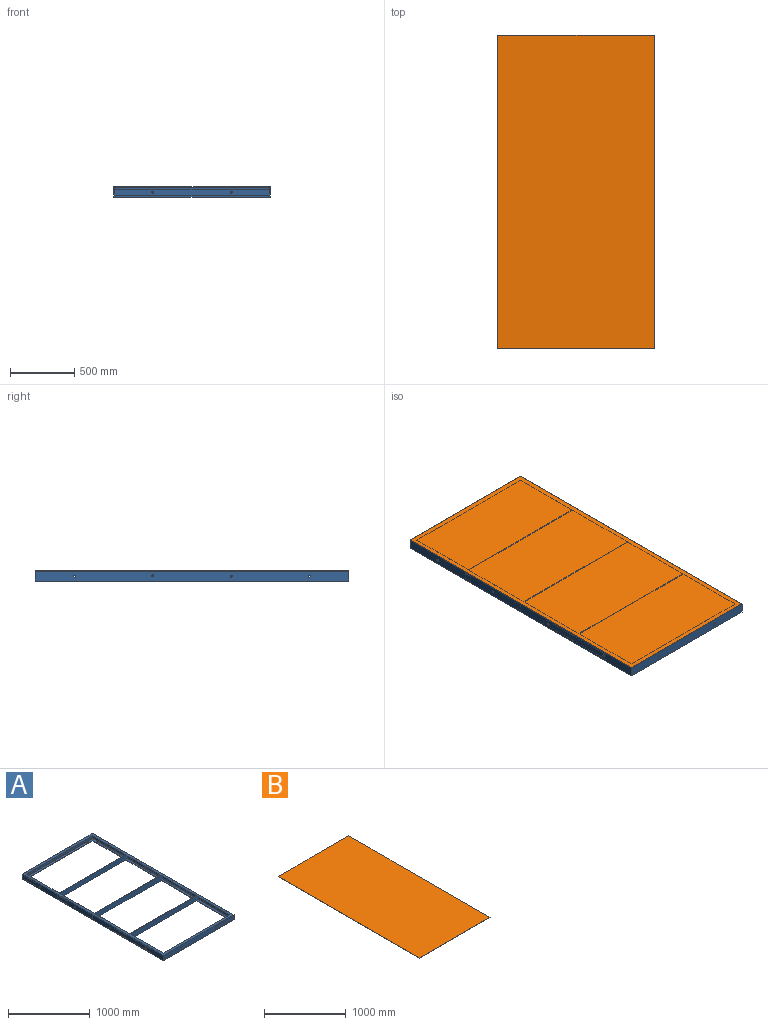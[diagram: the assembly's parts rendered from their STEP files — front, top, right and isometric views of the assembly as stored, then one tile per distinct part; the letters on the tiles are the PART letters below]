
ASSEMBLY  parts=2 mates=1
PART A: 122 faces, bbox 1219.4x2438.6x76.4 mm
  f0: cylinder r=2.54mm len=603.25mm, axis (0,1,0), area 2155.3mm2, adj f1,f8,f110,f113
  f1: plane 603.25x23.69mm, normal (0.16,0,-0.99), area 14489.9mm2, adj f0,f2,f110,f113
  f2: cylinder r=6.86mm len=603.25mm, axis (0,1,0), area 5814.6mm2, adj f1,f3,f110,f113
  f3: plane 603.25x45.45mm, normal (1,0,0), area 27220.2mm2, adj f2,f4,f106,f110,f113
  f4: cylinder r=6.86mm len=603.25mm, axis (0,1,0), area 5814.6mm2, adj f3,f5,f110,f113
  f5: plane 603.25x23.69mm, normal (0.16,0,0.99), area 14489.9mm2, adj f4,f6,f110,f113
  f6: cylinder r=2.54mm len=603.25mm, axis (0,1,0), area 2155.3mm2, adj f5,f7,f110,f113
  f7: plane 603.25x2.16mm, normal (1,0,0), area 1300.9mm2, adj f6,f64,f110,f113
  f8: plane 603.25x2.16mm, normal (1,0,0), area 1300.9mm2, adj f0,f66,f110,f113
  f9: cylinder r=2.54mm len=603.25mm, axis (0,-1,0), area 2155.3mm2, adj f10,f17,f110,f113
  f10: plane 603.25x23.69mm, normal (-0.16,0,-0.99), area 14489.9mm2, adj f9,f11,f110,f113
  f11: cylinder r=6.86mm len=603.25mm, axis (0,-1,0), area 5814.6mm2, adj f10,f12,f110,f113
  f12: plane 603.25x45.45mm, normal (-1,0,0), area 27220.2mm2, adj f11,f13,f102,f110,f113
  f13: cylinder r=6.86mm len=603.25mm, axis (0,-1,0), area 5814.6mm2, adj f12,f14,f110,f113
  f14: plane 603.25x23.69mm, normal (-0.16,0,0.99), area 14489.9mm2, adj f13,f15,f110,f113
  f15: cylinder r=2.54mm len=603.25mm, axis (0,-1,0), area 2155.3mm2, adj f14,f16,f110,f113
  f16: plane 603.25x2.16mm, normal (-1,0,0), area 1300.9mm2, adj f15,f64,f110,f113
  f17: plane 603.25x2.16mm, normal (-1,0,0), area 1300.9mm2, adj f9,f66,f110,f113
  f18: cylinder r=2.54mm len=603.25mm, axis (0,1,0), area 2155.3mm2, adj f19,f26,f108,f111
  f19: plane 603.25x23.69mm, normal (0.16,0,-0.99), area 14489.9mm2, adj f18,f20,f108,f111
  f20: cylinder r=6.86mm len=603.25mm, axis (0,1,0), area 5814.6mm2, adj f19,f21,f108,f111
  f21: plane 603.25x45.45mm, normal (1,0,0), area 27220.2mm2, adj f20,f22,f105,f108,f111
  f22: cylinder r=6.86mm len=603.25mm, axis (0,1,0), area 5814.6mm2, adj f21,f23,f108,f111
  f23: plane 603.25x23.69mm, normal (0.16,0,0.99), area 14489.9mm2, adj f22,f24,f108,f111
  f24: cylinder r=2.54mm len=603.25mm, axis (0,1,0), area 2155.3mm2, adj f23,f25,f108,f111
  f25: plane 603.25x2.16mm, normal (1,0,0), area 1300.9mm2, adj f24,f64,f108,f111
  f26: plane 603.25x2.16mm, normal (1,0,0), area 1300.9mm2, adj f18,f66,f108,f111
  f27: cylinder r=2.54mm len=603.25mm, axis (0,-1,0), area 2155.3mm2, adj f28,f35,f108,f111
  f28: plane 603.25x23.69mm, normal (-0.16,0,-0.99), area 14489.9mm2, adj f27,f29,f108,f111
  f29: cylinder r=6.86mm len=603.25mm, axis (0,-1,0), area 5814.6mm2, adj f28,f30,f108,f111
  f30: plane 603.25x45.45mm, normal (-1,0,0), area 27220.2mm2, adj f29,f31,f101,f108,f111
  f31: cylinder r=6.86mm len=603.25mm, axis (0,-1,0), area 5814.6mm2, adj f30,f32,f108,f111
  f32: plane 603.25x23.69mm, normal (-0.16,0,0.99), area 14489.9mm2, adj f31,f33,f108,f111
  f33: cylinder r=2.54mm len=603.25mm, axis (0,-1,0), area 2155.3mm2, adj f32,f34,f108,f111
  f34: plane 603.25x2.16mm, normal (-1,0,0), area 1300.9mm2, adj f33,f64,f108,f111
  f35: plane 603.25x2.16mm, normal (-1,0,0), area 1300.9mm2, adj f27,f66,f108,f111
  f36: cylinder r=2.54mm len=573.62mm, axis (0,1,0), area 2044.6mm2, adj f37,f44,f74,f109
  f37: plane 597.32x23.69mm, normal (0.16,0,-0.99), area 14062.8mm2, adj f36,f38,f73,f109
  f38: cylinder r=6.86mm len=603.05mm, axis (0,1,0), area 5792.9mm2, adj f37,f39,f72,f109
  f39: plane 603.05x45.45mm, normal (1,0,0), area 27211mm2, adj f38,f40,f71,f107,f109
  f40: cylinder r=6.86mm len=603.05mm, axis (0,1,0), area 5786.1mm2, adj f39,f41,f70,f109,f119
  f41: plane 597.48x23.86mm, normal (0.16,0,0.99), area 13868.8mm2, adj f40,f42,f69,f109,f119
  f42: cylinder r=2.54mm len=573.62mm, axis (0,1,0), area 2044.6mm2, adj f41,f43,f68,f109
  f43: plane 571.5x2.16mm, normal (1,0,0), area 1232.4mm2, adj f42,f64,f76,f109
  f44: plane 571.5x2.16mm, normal (1,0,0), area 1232.4mm2, adj f36,f66,f75,f109
  f45: cylinder r=2.54mm len=573.62mm, axis (0,-1,0), area 2044.6mm2, adj f46,f53,f74,f109
  f46: plane 597.32x23.69mm, normal (-0.16,0,-0.99), area 14062.8mm2, adj f45,f47,f73,f109
  f47: cylinder r=6.86mm len=603.05mm, axis (0,-1,0), area 5792.9mm2, adj f46,f48,f72,f109
  f48: plane 603.05x45.45mm, normal (-1,0,0), area 27211mm2, adj f47,f49,f71,f103,f109
  f49: cylinder r=6.86mm len=603.05mm, axis (0,-1,0), area 5786.1mm2, adj f48,f50,f70,f109,f121
  f50: plane 597.48x23.86mm, normal (-0.16,0,0.99), area 13868.8mm2, adj f49,f51,f69,f109,f121
  f51: cylinder r=2.54mm len=573.62mm, axis (0,-1,0), area 2044.6mm2, adj f50,f52,f68,f109
  f52: plane 571.5x2.16mm, normal (-1,0,0), area 1232.4mm2, adj f51,f64,f76,f109
  f53: plane 571.5x2.16mm, normal (-1,0,0), area 1232.4mm2, adj f45,f66,f75,f109
  f54: plane 1219.2x76.2mm, normal (0,-1,0), area 92507.2mm2, adj f64,f65,f66,f94,f98,f99
  f55: plane 1219.2x76.2mm, normal (0,1,0), area 92507.2mm2, adj f64,f65,f66,f94,f96,f97
  f56: cylinder r=2.54mm len=567.27mm, axis (0,1,0), area 2021.9mm2, adj f57,f67,f77,f112
  f57: plane 590.97x23.69mm, normal (0.16,0,-0.99), area 13910.3mm2, adj f56,f58,f78,f112
  f58: cylinder r=6.86mm len=596.7mm, axis (0,1,0), area 5731.7mm2, adj f57,f59,f79,f112
  f59: plane 596.7x45.45mm, normal (1,0,0), area 26922.4mm2, adj f58,f60,f80,f104,f112
  f60: cylinder r=6.86mm len=596.7mm, axis (0,1,0), area 5724.9mm2, adj f59,f61,f81,f112,f120
  f61: plane 591.13x23.86mm, normal (0.16,0,0.99), area 13716.3mm2, adj f60,f62,f82,f112,f120
  f62: cylinder r=2.54mm len=567.27mm, axis (0,1,0), area 2021.9mm2, adj f61,f63,f83,f112
  f63: plane 565.15x2.16mm, normal (1,0,0), area 1218.7mm2, adj f62,f64,f84,f112
  f64: plane 2438.4x1219.2mm, normal (0,0,-1), area 293093.4mm2, adj f7,f16,f25,f34,f43,f52,f54,f55
  f65: plane 2438.4x76.2mm, normal (-1,0,0), area 185014.3mm2, adj f54,f55,f64,f66,f104,f105,f106,f107
  f66: plane 2438.4x1219.2mm, normal (0,0,1), area 294676.8mm2, adj f8,f17,f26,f35,f44,f53,f54,f55
  f67: plane 565.15x2.16mm, normal (1,0,0), area 1218.7mm2, adj f56,f66,f85,f112
  f68: cylinder r=2.54mm len=1147.25mm, axis (1,0,0), area 4089.2mm2, adj f42,f51,f69,f76
  f69: plane 1194.63x23.69mm, normal (0,0.16,0.99), area 27737.6mm2, adj f41,f50,f68,f70,f117,f118
  f70: cylinder r=6.86mm len=1206.09mm, axis (1,0,0), area 11572.3mm2, adj f40,f49,f69,f71,f117,f118
  f71: plane 1206.09x45.45mm, normal (0,1,0), area 54422mm2, adj f39,f48,f70,f72,f98,f99
  f72: cylinder r=6.86mm len=1206.09mm, axis (1,0,0), area 11585.8mm2, adj f38,f47,f71,f73
  f73: plane 1194.63x23.69mm, normal (0,0.16,-0.99), area 28125.6mm2, adj f37,f46,f72,f74
  f74: cylinder r=2.54mm len=1147.25mm, axis (1,0,0), area 4089.2mm2, adj f36,f45,f73,f75
  f75: plane 1143x2.16mm, normal (0,1,0), area 2464.8mm2, adj f44,f53,f66,f74
  f76: plane 1143x2.16mm, normal (0,1,0), area 2464.8mm2, adj f43,f52,f64,f68
  f77: cylinder r=2.54mm len=1147.25mm, axis (1,0,0), area 4089.2mm2, adj f56,f78,f85,f86
  f78: plane 1194.63x23.69mm, normal (0,-0.16,-0.99), area 28125.6mm2, adj f57,f77,f79,f87
  f79: cylinder r=6.86mm len=1206.09mm, axis (1,0,0), area 11585.8mm2, adj f58,f78,f80,f88
  f80: plane 1206.09x45.45mm, normal (0,-1,0), area 54422mm2, adj f59,f79,f81,f89,f96,f97
  f81: cylinder r=6.86mm len=1206.09mm, axis (1,0,0), area 11572.3mm2, adj f60,f80,f82,f90,f115,f116
  f82: plane 1194.63x23.69mm, normal (0,-0.16,0.99), area 27737.6mm2, adj f61,f81,f83,f91,f115,f116
  f83: cylinder r=2.54mm len=1147.25mm, axis (1,0,0), area 4089.2mm2, adj f62,f82,f84,f92
  f84: plane 1143x2.16mm, normal (0,-1,0), area 2464.8mm2, adj f63,f64,f83,f93
  f85: plane 1143x2.16mm, normal (0,-1,0), area 2464.8mm2, adj f66,f67,f77,f95
  f86: cylinder r=2.54mm len=567.27mm, axis (0,-1,0), area 2021.9mm2, adj f77,f87,f95,f112
  f87: plane 590.97x23.69mm, normal (-0.16,0,-0.99), area 13910.3mm2, adj f78,f86,f88,f112
  f88: cylinder r=6.86mm len=596.7mm, axis (0,-1,0), area 5731.7mm2, adj f79,f87,f89,f112
  f89: plane 596.7x45.45mm, normal (-1,0,0), area 26922.4mm2, adj f80,f88,f90,f100,f112
  f90: cylinder r=6.86mm len=596.7mm, axis (0,-1,0), area 5724.9mm2, adj f81,f89,f91,f112,f114
  f91: plane 591.13x23.86mm, normal (-0.16,0,0.99), area 13716.3mm2, adj f82,f90,f92,f112,f114
  f92: cylinder r=2.54mm len=567.27mm, axis (0,-1,0), area 2021.9mm2, adj f83,f91,f93,f112
  f93: plane 565.15x2.16mm, normal (-1,0,0), area 1218.7mm2, adj f64,f84,f92,f112
  f94: plane 2438.4x76.2mm, normal (1,0,0), area 185014.3mm2, adj f54,f55,f64,f66,f100,f101,f102,f103
  f95: plane 565.15x2.16mm, normal (-1,0,0), area 1218.7mm2, adj f66,f85,f86,f112
  f96: cylinder r=7.94mm len=15.88mm, axis (0,-1,0), area 326.8mm2, adj f55,f80
  f97: cylinder r=7.94mm len=15.88mm, axis (0,-1,0), area 326.8mm2, adj f55,f80
  f98: cylinder r=7.94mm len=15.88mm, axis (0,-1,0), area 326.8mm2, adj f54,f71
  f99: cylinder r=7.94mm len=15.88mm, axis (0,-1,0), area 326.8mm2, adj f54,f71
  f100: cylinder r=7.94mm len=15.88mm, axis (1,0,0), area 326.8mm2, adj f89,f94
  f101: cylinder r=7.94mm len=15.88mm, axis (1,0,0), area 326.8mm2, adj f30,f94
  f102: cylinder r=7.94mm len=15.88mm, axis (1,0,0), area 326.8mm2, adj f12,f94
  f103: cylinder r=7.94mm len=15.88mm, axis (1,0,0), area 326.8mm2, adj f48,f94
  f104: cylinder r=7.94mm len=15.88mm, axis (1,0,0), area 326.8mm2, adj f59,f65
  f105: cylinder r=7.94mm len=15.88mm, axis (1,0,0), area 326.8mm2, adj f21,f65
  f106: cylinder r=7.94mm len=15.88mm, axis (1,0,0), area 326.8mm2, adj f3,f65
  f107: cylinder r=7.94mm len=15.88mm, axis (1,0,0), area 326.8mm2, adj f39,f65
  f108: plane 1206.09x76.2mm, normal (0,1,0), area 91005.5mm2, adj f18,f19,f20,f21,f22,f23,f24,f25
  f109: plane 1206.09x76.2mm, normal (0,-1,0), area 91005.5mm2, adj f36,f37,f38,f39,f40,f41,f42,f43
  f110: plane 1206.09x76.2mm, normal (0,1,0), area 91005.5mm2, adj f0,f1,f2,f3,f4,f5,f6,f7
  f111: plane 1206.09x76.2mm, normal (0,-1,0), area 91005.5mm2, adj f18,f19,f20,f21,f22,f23,f24,f25
  f112: plane 1206.09x76.2mm, normal (0,1,0), area 91005.5mm2, adj f56,f57,f58,f59,f60,f61,f62,f63
  f113: plane 1206.09x76.2mm, normal (0,-1,0), area 91005.5mm2, adj f0,f1,f2,f3,f4,f5,f6,f7
  f114: cylinder r=7.94mm len=15.88mm, axis (0,0,-1), area 373.3mm2, adj f64,f90,f91
  f115: cylinder r=7.94mm len=15.88mm, axis (0,0,-1), area 373.4mm2, adj f64,f81,f82
  f116: cylinder r=7.94mm len=15.88mm, axis (0,0,-1), area 373.4mm2, adj f64,f81,f82
  f117: cylinder r=7.94mm len=15.88mm, axis (0,0,-1), area 373.7mm2, adj f64,f69,f70
  f118: cylinder r=7.94mm len=15.88mm, axis (0,0,-1), area 373.7mm2, adj f64,f69,f70
  f119: cylinder r=7.94mm len=15.88mm, axis (0,0,-1), area 373.3mm2, adj f40,f41,f64
  f120: cylinder r=7.94mm len=15.88mm, axis (0,0,-1), area 373.3mm2, adj f60,f61,f64
  f121: cylinder r=7.94mm len=15.88mm, axis (0,0,-1), area 373.3mm2, adj f49,f50,f64
PART B: 6 faces, bbox 1219.2x2438.4x3.2 mm
  f0: plane 2438.4x3.18mm, normal (-1,0,0), area 7741.9mm2, adj f1,f3,f4,f5
  f1: plane 1219.2x3.18mm, normal (0,-1,0), area 3871mm2, adj f0,f2,f4,f5
  f2: plane 2438.4x3.18mm, normal (1,0,0), area 7741.9mm2, adj f1,f3,f4,f5
  f3: plane 1219.2x3.18mm, normal (0,1,0), area 3871mm2, adj f0,f2,f4,f5
  f4: plane 2438.4x1219.2mm, normal (0,0,1), area 2972897.3mm2, adj f0,f1,f2,f3
  f5: plane 2438.4x1219.2mm, normal (0,0,-1), area 2972897.3mm2, adj f0,f1,f2,f3
PLACE A rot(axis=(0,0.27,0.96),0deg) t=(0,0,0)mm
PLACE B rot(axis=(0,0.13,0.99),0deg) t=(0,0,0)mm
MATE fastened B.f5 <-> A.f66  axis (0,0,-1) through (0,0,0)mm
